# Revit family: 94535109
name_source: partatom
category: Equipamentos hidráulicos
revit_build: Autodesk Revit 2016 (Build: 20150220_1215(x64)
units: mm (PartAtom-declared; Revit-internal decimal feet)

## family parameters
Com base no plano de trabalho = Não
Compartilhado = Não
Corte com vazios quando carregados = Não
Cota do conector redondo = Utilizar diâmetro
Ponto de cálculo do ambiente = Não
Sempre na vertical = Sim
Tipo de parte = Normal

## types (1)
- Ralo Slim Tramontina - 94535/109
    Código de montagem = Ralo Slim Tramontina - 94535/109
    Descrição = Ralo Slim Tramontina - 94535/109
    Desenvolvedor = Factory Cursos
    Diametro do cano de saida = 40  [stored 0.131234 ft]
    Dimensões = 900 x 700 x 33
    Fabricante = Tramontina
    Manual de Instalação = <Nenhum>
    Modelo = Ralo Slim Tramontina - 94535/109
    Site do desenvolvedor = www.factorycursos.com.br
    Tipo de imagem = <Nenhum>
    URL = www.tramontina.com.br

note: [stored X ft] marks values corroborated as IEEE doubles in the binary element streams (Revit-internal decimal feet)
